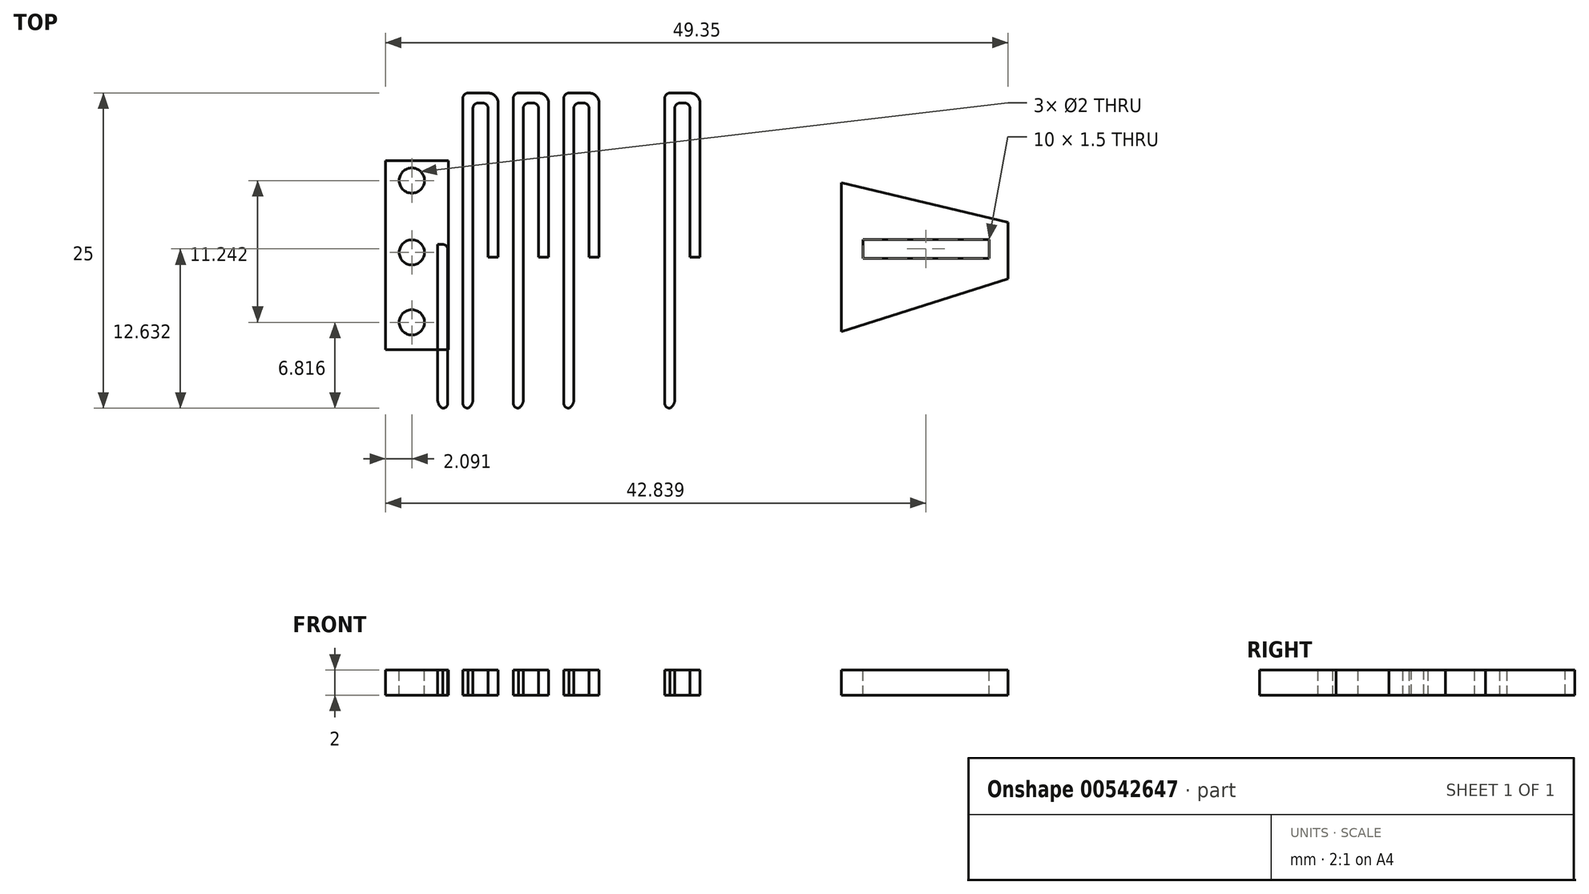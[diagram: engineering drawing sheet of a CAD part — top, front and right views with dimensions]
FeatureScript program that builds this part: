
annotation { "Feature Type Name" : "Feature", "Feature Type Description" : "" }
export const myFeature = defineFeature(function(context is Context, id is Id, definition is map)
    precondition{}
    {
        {
            var Q0;
            Q0=qCreatedBy(makeId("Top.planeOp"),FACE);
            var sketch = newSketch(context, id + "F0", { "sketchPlane" : qUnion([Q0])});
            skLineSegment(sketch, "E0", {"start": v(8.58, 13.23) * mm, "end": v(8.58, 25.43) * mm});
            skLineSegment(sketch, "E1", {"start": v(8.58, 25.43) * mm, "end": v(7.38, 25.43) * mm});
            skLineSegment(sketch, "E2", {"start": v(7.38, 25.43) * mm, "end": v(7.38, 1.23) * mm});
            skLineSegment(sketch, "E3", {"start": v(7.38, 1.23) * mm, "end": v(4.58, 1.23) * mm});
            skLineSegment(sketch, "E4", {"start": v(4.58, 1.23) * mm, "end": v(4.58, 14.23) * mm});
            skLineSegment(sketch, "E5", {"start": v(4.58, 14.23) * mm, "end": v(5.38, 14.23) * mm});
            skLineSegment(sketch, "E6", {"start": v(5.38, 14.23) * mm, "end": v(5.38, 1.23) * mm});
            skLineSegment(sketch, "E7", {"start": v(5.38, 1.23) * mm, "end": v(6.58, 1.23) * mm});
            skLineSegment(sketch, "E8", {"start": v(6.58, 1.23) * mm, "end": v(6.58, 26.23) * mm});
            skLineSegment(sketch, "E9", {"start": v(6.58, 26.23) * mm, "end": v(9.38, 26.23) * mm});
            skLineSegment(sketch, "E10", {"start": v(9.38, 26.23) * mm, "end": v(9.38, 13.23) * mm});
            skLineSegment(sketch, "E11", {"start": v(8.58, 13.23) * mm, "end": v(9.38, 13.23) * mm});
            skLineSegment(sketch, "E12", {"start": v(5.38, 2.03) * mm, "end": v(6.58, 2.03) * mm});
            skSolve(sketch);
        }
        {
            var Q0;
            Q0=makeQuery(id+"F0.imprint","IMPRINT",FACE,{"disambiguationData":[TD([[makeQuery(id+"F0.imprint","IMPRINT",EDGE,{"derivedFrom":sQuery(id+"F0.wireOp",EDGE,"E0")}),-1.0]])]});
            var Q1;
            {var subQ3=sQuery(id+"F0.wireOp",EDGE,"E4");Q1=makeQuery(id+"F0.imprint","IMPRINT",FACE,{"disambiguationData":[TD([[makeQuery(id+"F0.imprint","IMPRINT",EDGE,{"derivedFrom":subQ3}),-1.0]])]});}
            var Q2;
            {var subQ0=sQuery(id+"F0.wireOp",EDGE,"E7");Q2=makeQuery(id+"F0.imprint","IMPRINT",FACE,{"disambiguationData":[TD([[makeQuery(id+"F0.imprint","IMPRINT",EDGE,{"derivedFrom":subQ0}),1.0]])]});}
            extrude(context, id + "F1", {"entities" : qUnion([Q0, Q1, Q2]), "depth" : 2 * mm, "offsetDistance" : 25 * mm});
        }
        {
            var Q0;
            Q0=makeQuery(id+"F1.opExtrude","SWEPT_EDGE",EDGE,{"disambiguationData":[OSD([sQuery(id+"F0.wireOp",EDGE,"E1"),sQuery(id+"F0.wireOp",EDGE,"E2")])]});
            var Q1;
            Q1=makeQuery(id+"F1.opExtrude","SWEPT_EDGE",EDGE,{"disambiguationData":[OSD([sQuery(id+"F0.wireOp",EDGE,"E0"),sQuery(id+"F0.wireOp",EDGE,"E1")])]});
            var Q2;
            Q2=makeQuery(id+"F1.opExtrude","SWEPT_EDGE",EDGE,{"disambiguationData":[OSD([sQuery(id+"F0.wireOp",EDGE,"E6"),sQuery(id+"F0.wireOp",EDGE,"E7")])]});
            var Q3;
            Q3=makeQuery(id+"F1.opExtrude","SWEPT_EDGE",EDGE,{"disambiguationData":[OSD([sQuery(id+"F0.wireOp",EDGE,"E7"),sQuery(id+"F0.wireOp",EDGE,"E8")])]});
            fillet(context, id + "F2", {"entities" : qUnion([Q0, Q1, Q2, Q3]), "radius" : .4 * mm, "tangentPropagation" : true, "allowEdgeOverflow" : false});
        }
        {
            var Q0;
            Q0=makeQuery(id+"F1.opExtrude","SWEPT_EDGE",EDGE,{"disambiguationData":[OSD([sQuery(id+"F0.wireOp",EDGE,"E8"),sQuery(id+"F0.wireOp",EDGE,"E9")])]});
            var Q1;
            Q1=makeQuery(id+"F1.opExtrude","SWEPT_EDGE",EDGE,{"disambiguationData":[OSD([sQuery(id+"F0.wireOp",EDGE,"E9"),sQuery(id+"F0.wireOp",EDGE,"E10")])]});
            var Q2;
            Q2=makeQuery(id+"F1.opExtrude","SWEPT_EDGE",EDGE,{"disambiguationData":[OSD([sQuery(id+"F0.wireOp",EDGE,"E2"),sQuery(id+"F0.wireOp",EDGE,"E3")])]});
            var Q3;
            Q3=makeQuery(id+"F1.opExtrude","SWEPT_EDGE",EDGE,{"disambiguationData":[OSD([sQuery(id+"F0.wireOp",EDGE,"E3"),sQuery(id+"F0.wireOp",EDGE,"E4")])]});
            fillet(context, id + "F3", {"entities" : qUnion([Q0, Q1, Q2, Q3]), "radius" : .8 * mm, "tangentPropagation" : true, "allowEdgeOverflow" : false});
        }
        {
            var Q0;
            Q0=makeQuery(id+"F1.opExtrude","SWEPT_BODY",BODY,{"disambiguationData":[OSD([sQuery(id+"F0.wireOp",EDGE,"E0"),sQuery(id+"F0.wireOp",EDGE,"E1"),sQuery(id+"F0.wireOp",EDGE,"E2"),sQuery(id+"F0.wireOp",EDGE,"E3"),sQuery(id+"F0.wireOp",EDGE,"E4"),sQuery(id+"F0.wireOp",EDGE,"E5"),sQuery(id+"F0.wireOp",EDGE,"E6"),sQuery(id+"F0.wireOp",EDGE,"E7"),sQuery(id+"F0.wireOp",EDGE,"E8"),sQuery(id+"F0.wireOp",EDGE,"E9"),sQuery(id+"F0.wireOp",EDGE,"E10"),sQuery(id+"F0.wireOp",EDGE,"E11")])]});
            transform(context, id + "F4", {"entities" : qUnion([Q0]), "transformType" : TransformType.TRANSLATION_3D, "dx" : 4 * mm, "dy" : 0 * mm, "dz" : 0 * mm, "makeCopy" : true});
        }
        {
            var Q0;
            Q0=makeQuery(id+"F1.opExtrude","SWEPT_BODY",BODY,{"disambiguationData":[OSD([sQuery(id+"F0.wireOp",EDGE,"E0"),sQuery(id+"F0.wireOp",EDGE,"E1"),sQuery(id+"F0.wireOp",EDGE,"E2"),sQuery(id+"F0.wireOp",EDGE,"E3"),sQuery(id+"F0.wireOp",EDGE,"E4"),sQuery(id+"F0.wireOp",EDGE,"E5"),sQuery(id+"F0.wireOp",EDGE,"E6"),sQuery(id+"F0.wireOp",EDGE,"E7"),sQuery(id+"F0.wireOp",EDGE,"E8"),sQuery(id+"F0.wireOp",EDGE,"E9"),sQuery(id+"F0.wireOp",EDGE,"E10"),sQuery(id+"F0.wireOp",EDGE,"E11")])]});
            var Q1;
            Q1=makeQuery(id+"F4.opPattern","COPY",BODY,{"derivedFrom":makeQuery(id+"F1.opExtrude","SWEPT_BODY",BODY,{"disambiguationData":[OSD([sQuery(id+"F0.wireOp",EDGE,"E0"),sQuery(id+"F0.wireOp",EDGE,"E1"),sQuery(id+"F0.wireOp",EDGE,"E2"),sQuery(id+"F0.wireOp",EDGE,"E3"),sQuery(id+"F0.wireOp",EDGE,"E4"),sQuery(id+"F0.wireOp",EDGE,"E5"),sQuery(id+"F0.wireOp",EDGE,"E6"),sQuery(id+"F0.wireOp",EDGE,"E7"),sQuery(id+"F0.wireOp",EDGE,"E8"),sQuery(id+"F0.wireOp",EDGE,"E9"),sQuery(id+"F0.wireOp",EDGE,"E10"),sQuery(id+"F0.wireOp",EDGE,"E11")])]}),"instanceName":"1"});
            booleanBodies(context, id + "F5", {"operationType" : BooleanOperationType.UNION, "tools" : qUnion([Q0, Q1])});
        }
        {
            var Q0;
            Q0=makeQuery(id+"F1.opExtrude","SWEPT_BODY",BODY,{"disambiguationData":[OSD([sQuery(id+"F0.wireOp",EDGE,"E0"),sQuery(id+"F0.wireOp",EDGE,"E1"),sQuery(id+"F0.wireOp",EDGE,"E2"),sQuery(id+"F0.wireOp",EDGE,"E3"),sQuery(id+"F0.wireOp",EDGE,"E4"),sQuery(id+"F0.wireOp",EDGE,"E5"),sQuery(id+"F0.wireOp",EDGE,"E6"),sQuery(id+"F0.wireOp",EDGE,"E7"),sQuery(id+"F0.wireOp",EDGE,"E8"),sQuery(id+"F0.wireOp",EDGE,"E9"),sQuery(id+"F0.wireOp",EDGE,"E10"),sQuery(id+"F0.wireOp",EDGE,"E11")])]});
            transform(context, id + "F6", {"entities" : qUnion([Q0]), "transformType" : TransformType.TRANSLATION_3D, "dx" : 8 * mm, "dy" : 0 * mm, "dz" : 0 * mm, "makeCopy" : true});
        }
        {
            var Q0;
            Q0=makeQuery(id+"F1.opExtrude","SWEPT_BODY",BODY,{"disambiguationData":[OSD([sQuery(id+"F0.wireOp",EDGE,"E0"),sQuery(id+"F0.wireOp",EDGE,"E1"),sQuery(id+"F0.wireOp",EDGE,"E2"),sQuery(id+"F0.wireOp",EDGE,"E3"),sQuery(id+"F0.wireOp",EDGE,"E4"),sQuery(id+"F0.wireOp",EDGE,"E5"),sQuery(id+"F0.wireOp",EDGE,"E6"),sQuery(id+"F0.wireOp",EDGE,"E7"),sQuery(id+"F0.wireOp",EDGE,"E8"),sQuery(id+"F0.wireOp",EDGE,"E9"),sQuery(id+"F0.wireOp",EDGE,"E10"),sQuery(id+"F0.wireOp",EDGE,"E11")])]});
            var Q1;
            Q1=makeQuery(id+"F6.opPattern","COPY",BODY,{"derivedFrom":makeQuery(id+"F1.opExtrude","SWEPT_BODY",BODY,{"disambiguationData":[OSD([sQuery(id+"F0.wireOp",EDGE,"E0"),sQuery(id+"F0.wireOp",EDGE,"E1"),sQuery(id+"F0.wireOp",EDGE,"E2"),sQuery(id+"F0.wireOp",EDGE,"E3"),sQuery(id+"F0.wireOp",EDGE,"E4"),sQuery(id+"F0.wireOp",EDGE,"E5"),sQuery(id+"F0.wireOp",EDGE,"E6"),sQuery(id+"F0.wireOp",EDGE,"E7"),sQuery(id+"F0.wireOp",EDGE,"E8"),sQuery(id+"F0.wireOp",EDGE,"E9"),sQuery(id+"F0.wireOp",EDGE,"E10"),sQuery(id+"F0.wireOp",EDGE,"E11")])]}),"instanceName":"1"});
            booleanBodies(context, id + "F7", {"operationType" : BooleanOperationType.UNION, "tools" : qUnion([Q0, Q1])});
        }
        {
            var Q0;
            Q0=makeQuery(id+"F1.opExtrude","SWEPT_BODY",BODY,{"disambiguationData":[OSD([sQuery(id+"F0.wireOp",EDGE,"E0"),sQuery(id+"F0.wireOp",EDGE,"E1"),sQuery(id+"F0.wireOp",EDGE,"E2"),sQuery(id+"F0.wireOp",EDGE,"E3"),sQuery(id+"F0.wireOp",EDGE,"E4"),sQuery(id+"F0.wireOp",EDGE,"E5"),sQuery(id+"F0.wireOp",EDGE,"E6"),sQuery(id+"F0.wireOp",EDGE,"E7"),sQuery(id+"F0.wireOp",EDGE,"E8"),sQuery(id+"F0.wireOp",EDGE,"E9"),sQuery(id+"F0.wireOp",EDGE,"E10"),sQuery(id+"F0.wireOp",EDGE,"E11")])]});
            transform(context, id + "F8", {"entities" : qUnion([Q0]), "transformType" : TransformType.TRANSLATION_3D, "dx" : 16 * mm, "dy" : 0 * mm, "dz" : 0 * mm, "makeCopy" : true});
        }
        {
            var Q0;
            Q0=makeQuery(id+"F1.opExtrude","SWEPT_BODY",BODY,{"disambiguationData":[OSD([sQuery(id+"F0.wireOp",EDGE,"E0"),sQuery(id+"F0.wireOp",EDGE,"E1"),sQuery(id+"F0.wireOp",EDGE,"E2"),sQuery(id+"F0.wireOp",EDGE,"E3"),sQuery(id+"F0.wireOp",EDGE,"E4"),sQuery(id+"F0.wireOp",EDGE,"E5"),sQuery(id+"F0.wireOp",EDGE,"E6"),sQuery(id+"F0.wireOp",EDGE,"E7"),sQuery(id+"F0.wireOp",EDGE,"E8"),sQuery(id+"F0.wireOp",EDGE,"E9"),sQuery(id+"F0.wireOp",EDGE,"E10"),sQuery(id+"F0.wireOp",EDGE,"E11")])]});
            var Q1;
            Q1=makeQuery(id+"F8.opPattern","COPY",BODY,{"derivedFrom":makeQuery(id+"F1.opExtrude","SWEPT_BODY",BODY,{"disambiguationData":[OSD([sQuery(id+"F0.wireOp",EDGE,"E0"),sQuery(id+"F0.wireOp",EDGE,"E1"),sQuery(id+"F0.wireOp",EDGE,"E2"),sQuery(id+"F0.wireOp",EDGE,"E3"),sQuery(id+"F0.wireOp",EDGE,"E4"),sQuery(id+"F0.wireOp",EDGE,"E5"),sQuery(id+"F0.wireOp",EDGE,"E6"),sQuery(id+"F0.wireOp",EDGE,"E7"),sQuery(id+"F0.wireOp",EDGE,"E8"),sQuery(id+"F0.wireOp",EDGE,"E9"),sQuery(id+"F0.wireOp",EDGE,"E10"),sQuery(id+"F0.wireOp",EDGE,"E11")])]}),"instanceName":"1"});
            booleanBodies(context, id + "F9", {"operationType" : BooleanOperationType.UNION, "tools" : qUnion([Q0, Q1])});
        }
        {
            var Q0;
            {var subQ0=makeQuery(id+"F1.opExtrude","CAP_FACE",FACE,{"disambiguationData":[OSD([sQuery(id+"F0.wireOp",EDGE,"E0"),sQuery(id+"F0.wireOp",EDGE,"E1"),sQuery(id+"F0.wireOp",EDGE,"E2"),sQuery(id+"F0.wireOp",EDGE,"E3"),sQuery(id+"F0.wireOp",EDGE,"E4"),sQuery(id+"F0.wireOp",EDGE,"E5"),sQuery(id+"F0.wireOp",EDGE,"E6"),sQuery(id+"F0.wireOp",EDGE,"E7"),sQuery(id+"F0.wireOp",EDGE,"E8"),sQuery(id+"F0.wireOp",EDGE,"E9"),sQuery(id+"F0.wireOp",EDGE,"E10"),sQuery(id+"F0.wireOp",EDGE,"E11")])],"isStart":false});var subQ1=makeQuery(id+"F5.opBoolean","MERGE",FACE,{"derivedFrom":[subQ0,makeQuery(id+"F4.opPattern","COPY",FACE,{"derivedFrom":subQ0,"instanceName":"1"})]});var subQ2=makeQuery(id+"F7.opBoolean","MERGE",FACE,{"derivedFrom":[subQ1,makeQuery(id+"F6.opPattern","COPY",FACE,{"derivedFrom":subQ1,"instanceName":"1"})]});Q0=makeQuery(id+"F9.opBoolean","MERGE",FACE,{"derivedFrom":[subQ2,makeQuery(id+"F8.opPattern","COPY",FACE,{"derivedFrom":subQ2,"instanceName":"1"})]});}
            var sketch = newSketch(context, id + "F10", { "sketchPlane" : qUnion([Q0])});
            skLineSegment(sketch, "E13.bottom", {"start": v(5.45, 20.87) * mm, "end": v(0.45, 20.87) * mm});
            skLineSegment(sketch, "E13.top", {"start": v(5.45, 5.87) * mm, "end": v(0.45, 5.87) * mm});
            skLineSegment(sketch, "E13.left", {"start": v(5.45, 20.87) * mm, "end": v(5.45, 5.87) * mm});
            skLineSegment(sketch, "E13.right", {"start": v(0.45, 20.87) * mm, "end": v(0.45, 5.87) * mm});
            skSolve(sketch);
        }
        {
            var Q0;
            {var subQ3=sQuery(id+"F10.wireOp",EDGE,"E13.right");Q0=makeQuery(id+"F10.imprint","IMPRINT",FACE,{"disambiguationData":[TD([[makeQuery(id+"F10.imprint","IMPRINT",EDGE,{"derivedFrom":subQ3}),1.0]])]});}
            extrude(context, id + "F11", {"entities" : qUnion([Q0]), "oppositeDirection" : true, "depth" : 2 * mm, "offsetDistance" : 25 * mm});
        }
        {
            var Q0;
            Q0=makeQuery(id+"F1.opExtrude","SWEPT_BODY",BODY,{"disambiguationData":[OSD([sQuery(id+"F0.wireOp",EDGE,"E0"),sQuery(id+"F0.wireOp",EDGE,"E1"),sQuery(id+"F0.wireOp",EDGE,"E2"),sQuery(id+"F0.wireOp",EDGE,"E3"),sQuery(id+"F0.wireOp",EDGE,"E4"),sQuery(id+"F0.wireOp",EDGE,"E5"),sQuery(id+"F0.wireOp",EDGE,"E6"),sQuery(id+"F0.wireOp",EDGE,"E7"),sQuery(id+"F0.wireOp",EDGE,"E8"),sQuery(id+"F0.wireOp",EDGE,"E9"),sQuery(id+"F0.wireOp",EDGE,"E10"),sQuery(id+"F0.wireOp",EDGE,"E11")])]});
            var Q1;
            Q1=makeQuery(id+"F11.opExtrude","SWEPT_BODY",BODY,{"disambiguationData":[OSD([sQuery(id+"F0.wireOp",EDGE,"E4"),sQuery(id+"F10.wireOp",EDGE,"E13.bottom"),sQuery(id+"F10.wireOp",EDGE,"E13.top"),sQuery(id+"F10.wireOp",EDGE,"E13.right")])]});
            booleanBodies(context, id + "F12", {"operationType" : BooleanOperationType.UNION, "tools" : qUnion([Q0, Q1])});
        }
        {
            var Q0;
            {var subQ0=sQuery(id+"F0.wireOp",EDGE,"E12");var subQ1=sQuery(id+"F0.wireOp",EDGE,"E11");var subQ2=sQuery(id+"F0.wireOp",EDGE,"E10");var subQ3=sQuery(id+"F0.wireOp",EDGE,"E9");var subQ4=sQuery(id+"F0.wireOp",EDGE,"E8");var subQ5=sQuery(id+"F0.wireOp",EDGE,"E7");var subQ6=sQuery(id+"F0.wireOp",EDGE,"E6");var subQ7=sQuery(id+"F0.wireOp",EDGE,"E5");var subQ8=sQuery(id+"F0.wireOp",EDGE,"E4");var subQ9=sQuery(id+"F0.wireOp",EDGE,"E3");var subQ10=sQuery(id+"F0.wireOp",EDGE,"E2");var subQ11=sQuery(id+"F0.wireOp",EDGE,"E1");var subQ12=sQuery(id+"F0.wireOp",EDGE,"E0");var subQ13=makeQuery(id+"F1.opExtrude","CAP_FACE",FACE,{"disambiguationData":[OSD([subQ12,subQ11,subQ10,subQ9,subQ8,subQ7,subQ6,subQ5,subQ4,subQ3,subQ2,subQ1,subQ0])],"isStart":false});var subQ14=makeQuery(id+"F5.opBoolean","MERGE",FACE,{"derivedFrom":[subQ13,makeQuery(id+"F4.opPattern","COPY",FACE,{"derivedFrom":subQ13,"instanceName":"1"})]});var subQ15=makeQuery(id+"F7.opBoolean","MERGE",FACE,{"derivedFrom":[subQ14,makeQuery(id+"F6.opPattern","COPY",FACE,{"derivedFrom":subQ14,"instanceName":"1"})]});Q0=makeQuery(id+"F12.opBoolean","MERGE",FACE,{"derivedFrom":[makeQuery(id+"F9.opBoolean","MERGE",FACE,{"derivedFrom":[subQ15,makeQuery(id+"F8.opPattern","COPY",FACE,{"derivedFrom":subQ15,"instanceName":"1"})]}),makeQuery(id+"F11.opExtrude","CAP_FACE",FACE,{"disambiguationData":[OSD([subQ12,subQ11,subQ10,subQ9,subQ8,subQ7,subQ6,subQ5,subQ4,subQ3,subQ2,subQ1,subQ0,sQuery(id+"F10.wireOp",EDGE,"E13.bottom"),sQuery(id+"F10.wireOp",EDGE,"E13.top"),sQuery(id+"F10.wireOp",EDGE,"E13.left"),sQuery(id+"F10.wireOp",EDGE,"E13.right")])],"isStart":true})]});}
            var sketch = newSketch(context, id + "F13", { "sketchPlane" : qUnion([Q0])});
            skLineSegment(sketch, "E14", {"start": v(36.58, 19.13) * mm, "end": v(49.8, 15.97) * mm});
            skLineSegment(sketch, "E15", {"start": v(49.8, 15.97) * mm, "end": v(49.8, 11.48) * mm});
            skLineSegment(sketch, "E16", {"start": v(49.8, 11.48) * mm, "end": v(36.58, 7.31) * mm});
            skLineSegment(sketch, "E17", {"start": v(36.58, 7.31) * mm, "end": v(36.58, 19.13) * mm});
            skSolve(sketch);
        }
        {
            var Q0;
            {var subQ3=sQuery(id+"F13.wireOp",EDGE,"E15");Q0=makeQuery(id+"F13.imprint","IMPRINT",FACE,{"disambiguationData":[TD([[makeQuery(id+"F13.imprint","IMPRINT",EDGE,{"derivedFrom":subQ3}),-1.0]])]});}
            extrude(context, id + "F14", {"entities" : qUnion([Q0]), "operationType" : NewBodyOperationType.ADD, "oppositeDirection" : true, "depth" : 2 * mm, "offsetDistance" : 25 * mm});
        }
        {
            var Q0;
            {var subQ0=sQuery(id+"F0.wireOp",EDGE,"E4");var subQ1=makeQuery(id+"F1.opExtrude","CAP_FACE",FACE,{"disambiguationData":[OSD([sQuery(id+"F0.wireOp",EDGE,"E0"),sQuery(id+"F0.wireOp",EDGE,"E1"),sQuery(id+"F0.wireOp",EDGE,"E2"),sQuery(id+"F0.wireOp",EDGE,"E3"),subQ0,sQuery(id+"F0.wireOp",EDGE,"E5"),sQuery(id+"F0.wireOp",EDGE,"E6"),sQuery(id+"F0.wireOp",EDGE,"E7"),sQuery(id+"F0.wireOp",EDGE,"E8"),sQuery(id+"F0.wireOp",EDGE,"E9"),sQuery(id+"F0.wireOp",EDGE,"E10"),sQuery(id+"F0.wireOp",EDGE,"E11")])],"isStart":false});var subQ2=makeQuery(id+"F5.opBoolean","MERGE",FACE,{"derivedFrom":[subQ1,makeQuery(id+"F4.opPattern","COPY",FACE,{"derivedFrom":subQ1,"instanceName":"1"})]});var subQ3=makeQuery(id+"F7.opBoolean","MERGE",FACE,{"derivedFrom":[subQ2,makeQuery(id+"F6.opPattern","COPY",FACE,{"derivedFrom":subQ2,"instanceName":"1"})]});Q0=makeQuery(id+"F14.boolean.opBoolean","MERGE",FACE,{"derivedFrom":[makeQuery(id+"F12.opBoolean","MERGE",FACE,{"derivedFrom":[makeQuery(id+"F9.opBoolean","MERGE",FACE,{"derivedFrom":[subQ3,makeQuery(id+"F8.opPattern","COPY",FACE,{"derivedFrom":subQ3,"instanceName":"1"})]}),makeQuery(id+"F11.opExtrude","CAP_FACE",FACE,{"disambiguationData":[OSD([subQ0,sQuery(id+"F10.wireOp",EDGE,"E13.bottom"),sQuery(id+"F10.wireOp",EDGE,"E13.top"),sQuery(id+"F10.wireOp",EDGE,"E13.right")])],"isStart":true})]}),makeQuery(id+"F14.opExtrude","CAP_FACE",FACE,{"disambiguationData":[OSD([sQuery(id+"FsVnLeRDHpE6ryB_1.wireOp",EDGE,"sBowIyvc-GxD0-pyXb-HWLj-4zHhZNR5sUAh"),sQuery(id+"FsVnLeRDHpE6ryB_1.wireOp",EDGE,"usj1uOr3-hMyy-SFDE-oKVW-9Rd1Sj37hrVU"),sQuery(id+"FsVnLeRDHpE6ryB_1.wireOp",EDGE,"a70ZtGTO-GgWH-TJ9h-uHPC-t0WLluQc0GsC"),sQuery(id+"FsVnLeRDHpE6ryB_1.wireOp",EDGE,"40b8b113-d8ec-46b8-85d1-dfb4cab2dda9.filletArc")])],"isStart":true})]});}
            var sketch = newSketch(context, id + "F15", { "sketchPlane" : qUnion([Q0])});
            skCircle(sketch, "E18", {"center": v(2.54, 19.29) * mm, "radius": 1 * mm});
            skCircle(sketch, "E19", {"center": v(2.54, 13.59) * mm, "radius": 1 * mm});
            skCircle(sketch, "E20", {"center": v(2.54, 8.05) * mm, "radius": 1 * mm});
            skSolve(sketch);
        }
        {
            var Q0;
            Q0=makeQuery(id+"F15.imprint","IMPRINT",FACE,{"disambiguationData":[TD([[makeQuery(id+"F15.imprint","IMPRINT",EDGE,{"derivedFrom":sQuery(id+"F15.wireOp",EDGE,"E18")}),1.0]])]});
            var Q1;
            Q1=makeQuery(id+"F15.imprint","IMPRINT",FACE,{"disambiguationData":[TD([[makeQuery(id+"F15.imprint","IMPRINT",EDGE,{"derivedFrom":sQuery(id+"F15.wireOp",EDGE,"E19")}),1.0]])]});
            var Q2;
            Q2=makeQuery(id+"F15.imprint","IMPRINT",FACE,{"disambiguationData":[TD([[makeQuery(id+"F15.imprint","IMPRINT",EDGE,{"derivedFrom":sQuery(id+"F15.wireOp",EDGE,"E20")}),1.0]])]});
            extrude(context, id + "F16", {"entities" : qUnion([Q0, Q1, Q2]), "operationType" : NewBodyOperationType.REMOVE, "endBound" : BoundingType.THROUGH_ALL, "oppositeDirection" : true, "depth" : 25 * mm, "offsetDistance" : 25 * mm});
        }
        {
            var Q0;
            {var subQ0=sQuery(id+"F0.wireOp",EDGE,"E4");var subQ1=makeQuery(id+"F1.opExtrude","CAP_FACE",FACE,{"disambiguationData":[OSD([sQuery(id+"F0.wireOp",EDGE,"E0"),sQuery(id+"F0.wireOp",EDGE,"E1"),sQuery(id+"F0.wireOp",EDGE,"E2"),sQuery(id+"F0.wireOp",EDGE,"E3"),subQ0,sQuery(id+"F0.wireOp",EDGE,"E5"),sQuery(id+"F0.wireOp",EDGE,"E6"),sQuery(id+"F0.wireOp",EDGE,"E7"),sQuery(id+"F0.wireOp",EDGE,"E8"),sQuery(id+"F0.wireOp",EDGE,"E9"),sQuery(id+"F0.wireOp",EDGE,"E10"),sQuery(id+"F0.wireOp",EDGE,"E11")])],"isStart":false});var subQ2=makeQuery(id+"F5.opBoolean","MERGE",FACE,{"derivedFrom":[subQ1,makeQuery(id+"F4.opPattern","COPY",FACE,{"derivedFrom":subQ1,"instanceName":"1"})]});var subQ3=makeQuery(id+"F7.opBoolean","MERGE",FACE,{"derivedFrom":[subQ2,makeQuery(id+"F6.opPattern","COPY",FACE,{"derivedFrom":subQ2,"instanceName":"1"})]});Q0=makeQuery(id+"F14.boolean.opBoolean","MERGE",FACE,{"derivedFrom":[makeQuery(id+"F12.opBoolean","MERGE",FACE,{"derivedFrom":[makeQuery(id+"F9.opBoolean","MERGE",FACE,{"derivedFrom":[subQ3,makeQuery(id+"F8.opPattern","COPY",FACE,{"derivedFrom":subQ3,"instanceName":"1"})]}),makeQuery(id+"F11.opExtrude","CAP_FACE",FACE,{"disambiguationData":[OSD([subQ0,sQuery(id+"F10.wireOp",EDGE,"E13.bottom"),sQuery(id+"F10.wireOp",EDGE,"E13.top"),sQuery(id+"F10.wireOp",EDGE,"E13.right")])],"isStart":true})]}),makeQuery(id+"F14.opExtrude","CAP_FACE",FACE,{"disambiguationData":[OSD([sQuery(id+"FsVnLeRDHpE6ryB_1.wireOp",EDGE,"sBowIyvc-GxD0-pyXb-HWLj-4zHhZNR5sUAh"),sQuery(id+"FsVnLeRDHpE6ryB_1.wireOp",EDGE,"usj1uOr3-hMyy-SFDE-oKVW-9Rd1Sj37hrVU"),sQuery(id+"FsVnLeRDHpE6ryB_1.wireOp",EDGE,"a70ZtGTO-GgWH-TJ9h-uHPC-t0WLluQc0GsC"),sQuery(id+"FsVnLeRDHpE6ryB_1.wireOp",EDGE,"40b8b113-d8ec-46b8-85d1-dfb4cab2dda9.filletArc")])],"isStart":true})]});}
            var sketch = newSketch(context, id + "F17", { "sketchPlane" : qUnion([Q0])});
            skLineSegment(sketch, "E21.bottom", {"start": v(38.29, 14.61) * mm, "end": v(48.29, 14.61) * mm});
            skLineSegment(sketch, "E21.top", {"start": v(38.29, 13.11) * mm, "end": v(48.29, 13.11) * mm});
            skLineSegment(sketch, "E21.left", {"start": v(38.29, 14.61) * mm, "end": v(38.29, 13.11) * mm});
            skLineSegment(sketch, "E21.right", {"start": v(48.29, 14.61) * mm, "end": v(48.29, 13.11) * mm});
            skSolve(sketch);
        }
        {
            var Q0;
            Q0=makeQuery(id+"F17.imprint","IMPRINT",FACE,{"disambiguationData":[TD([[makeQuery(id+"F17.imprint","IMPRINT",EDGE,{"derivedFrom":sQuery(id+"F17.wireOp",EDGE,"E21.bottom")}),-1.0]])]});
            extrude(context, id + "F18", {"entities" : qUnion([Q0]), "operationType" : NewBodyOperationType.REMOVE, "endBound" : BoundingType.THROUGH_ALL, "oppositeDirection" : true, "depth" : 25 * mm, "offsetDistance" : 25 * mm});
        }
    });
